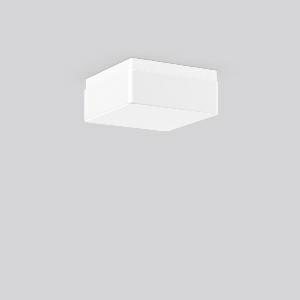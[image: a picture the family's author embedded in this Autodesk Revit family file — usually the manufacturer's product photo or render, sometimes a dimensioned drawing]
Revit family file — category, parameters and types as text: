
# Revit family: quadrat_20172_002_1df6
name_source: partatom
category: Lighting Fixtures
units: mm (PartAtom-declared; Revit-internal decimal feet)

## family parameters
Cut with Voids When Loaded = No
Host = Face
Light Source = No
Part Type = Normal
Room Calculation Point = No
Round Connector Dimension = Use Diameter
Shared = No

## types (1)
- QUADRAT (1 x QA60/clear E27, 1320 lm, 77 W, 3000)
    Apparent Load = 77 VA
    CIE Flux Codes = 34 63 85 72 42
    Color Rendering = 90
    Color Temperature = 3000
    Default Elevation = 1800 mm
    Description = Series: QUADRAT
Square surface-mounted luminaire in classic design. Base: plastic. Opal glass: mouth blown, silk finish. Diffuser fastening: spring system. Suitable for Ceiling mounting, Wall (surface). IP 43 ceiling mounting, IP 44 wall mounting. 
Colour: white
Length: 280 mm
Width: 280 mm
Height: 120 mm
Lamp: A60
Number of lamps: 1
Wattage: 100 W
Socket: E27
System power: 60 W
Rated luminous flux: 310 lm
Luminous efficiency: 5 lm/W
Control gear: Converter not necessary
Protection class: II
Type of protection: IP 43
    Height = 120 mm
    Lamp = 1 x QA60/clear E27
    Lamp Light Flux = 1320 lm
    Lamp Power = 77 W
    Lamp count = 1
    Length = 280 mm
    Lifetime = 3000 h
    Luminous efficacy = 7 lm/W
    Manufacturer = RZB
    ModVariant = No
    Model = 20172.002
    Mounting Place = Wall, Ceiling
    Mounting Type = Surface mounted
    Number of Poles = 1
    OnlyDefault = Yes
    Power Factor = 1
    Product Name = QUADRAT
    Product group = Surface mounted ceiling and wall luminaires
    ProductGroupID = 305
    Protection Class = Protection class II
    Protection Degree = IP 43
    RLX_Detail_Level = 1
    RLX_Emergency_Light_Flux = 0 lm
    RLX_Emergency_Type = 0
    RLX_Emergency_Type_DB = No
    RlxData = <blob elided: 11353 chars, md5=022ccbed>
    Socket = E27
    Standby Power = 0 W
    System Light Flux = 558 lm
    System Power = 77 W
    Type Comments = Product without accessories
    Type Image = 20129.002.jpg
    URL = http://relux.com
    VarID = ---
    Voltage = 230 V
    Voltage Range = 220-240 V
    Weight = 0.00 kg
    Width = 280 mm

## geometry (parser evidence)
native form markers: Sweep x12
no freeform markers — native parametric forms only
